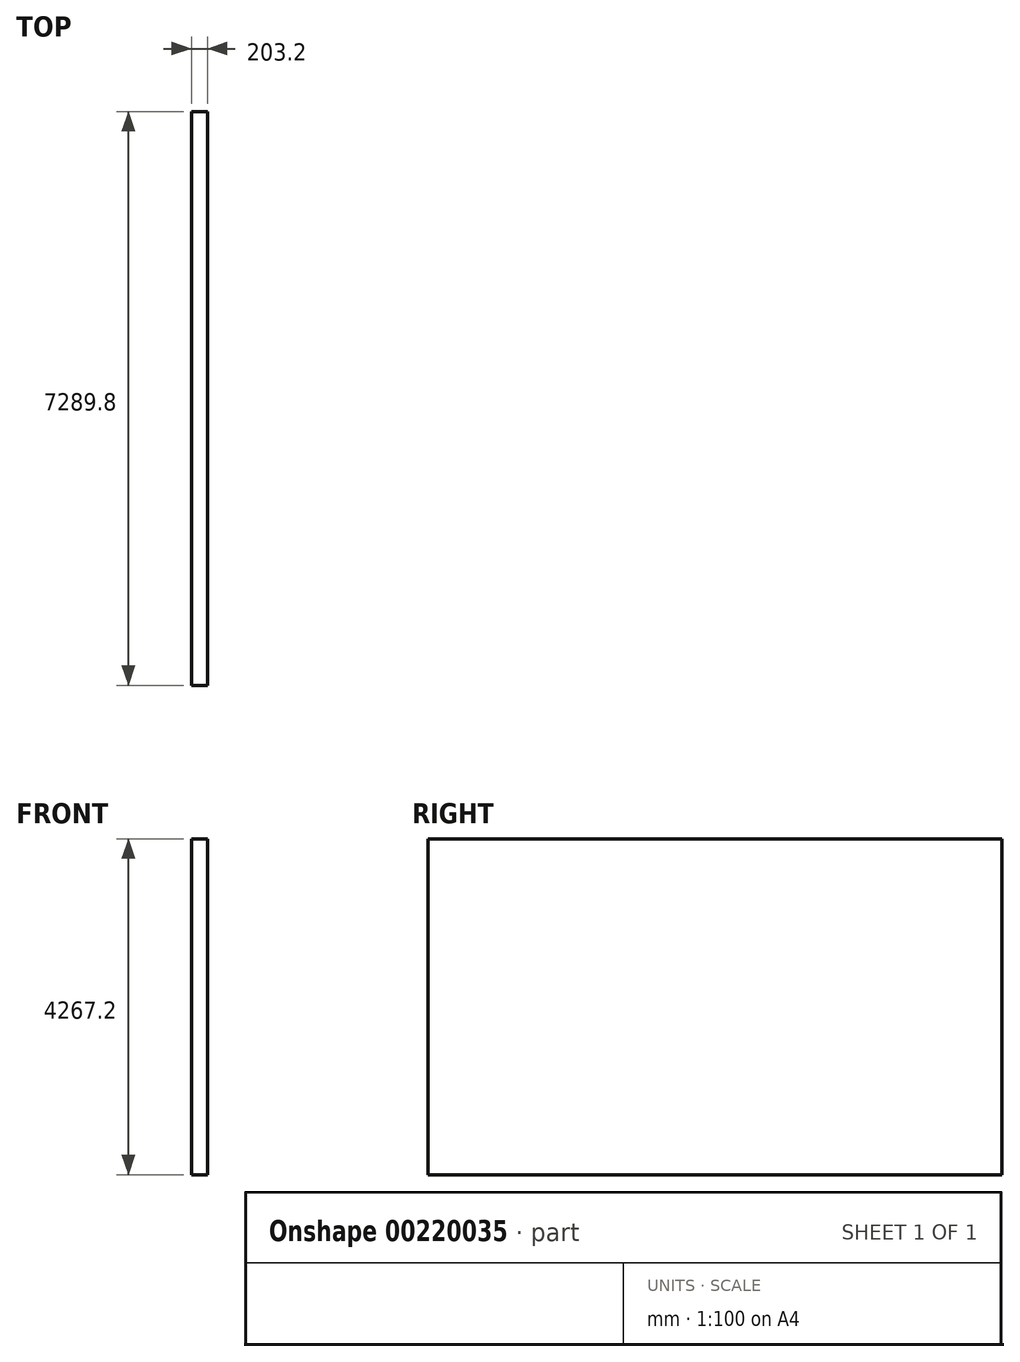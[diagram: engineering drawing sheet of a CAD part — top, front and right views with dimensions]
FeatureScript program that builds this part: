
annotation { "Feature Type Name" : "Feature", "Feature Type Description" : "" }
export const myFeature = defineFeature(function(context is Context, id is Id, definition is map)
    precondition{}
    {
        {
            var Q0;
            Q0=qCreatedBy(makeId("Right.planeOp"),FACE);
            var sketch = newSketch(context, id + "F0", { "sketchPlane" : qUnion([Q0])});
            skLineSegment(sketch, "E0.bottom", {"start": v(0, 0) * mm, "end": v(7289.8, 0) * mm});
            skLineSegment(sketch, "E0.top", {"start": v(0, 4267.2) * mm, "end": v(7289.8, 4267.2) * mm});
            skLineSegment(sketch, "E0.left", {"start": v(0, 0) * mm, "end": v(0, 4267.2) * mm});
            skLineSegment(sketch, "E0.right", {"start": v(7289.8, 0) * mm, "end": v(7289.8, 4267.2) * mm});
            skSolve(sketch);
        }
        {
            var Q0;
            Q0=makeQuery(id+"F0.imprint","IMPRINT",FACE,{"disambiguationData":[TD([[makeQuery(id+"F0.imprint","IMPRINT",EDGE,{"derivedFrom":sQuery(id+"F0.wireOp",EDGE,"E0.bottom")}),1.0]])]});
            extrude(context, id + "F1", {"entities" : qUnion([Q0]), "depth" : 203.2 * mm});
        }
    });
